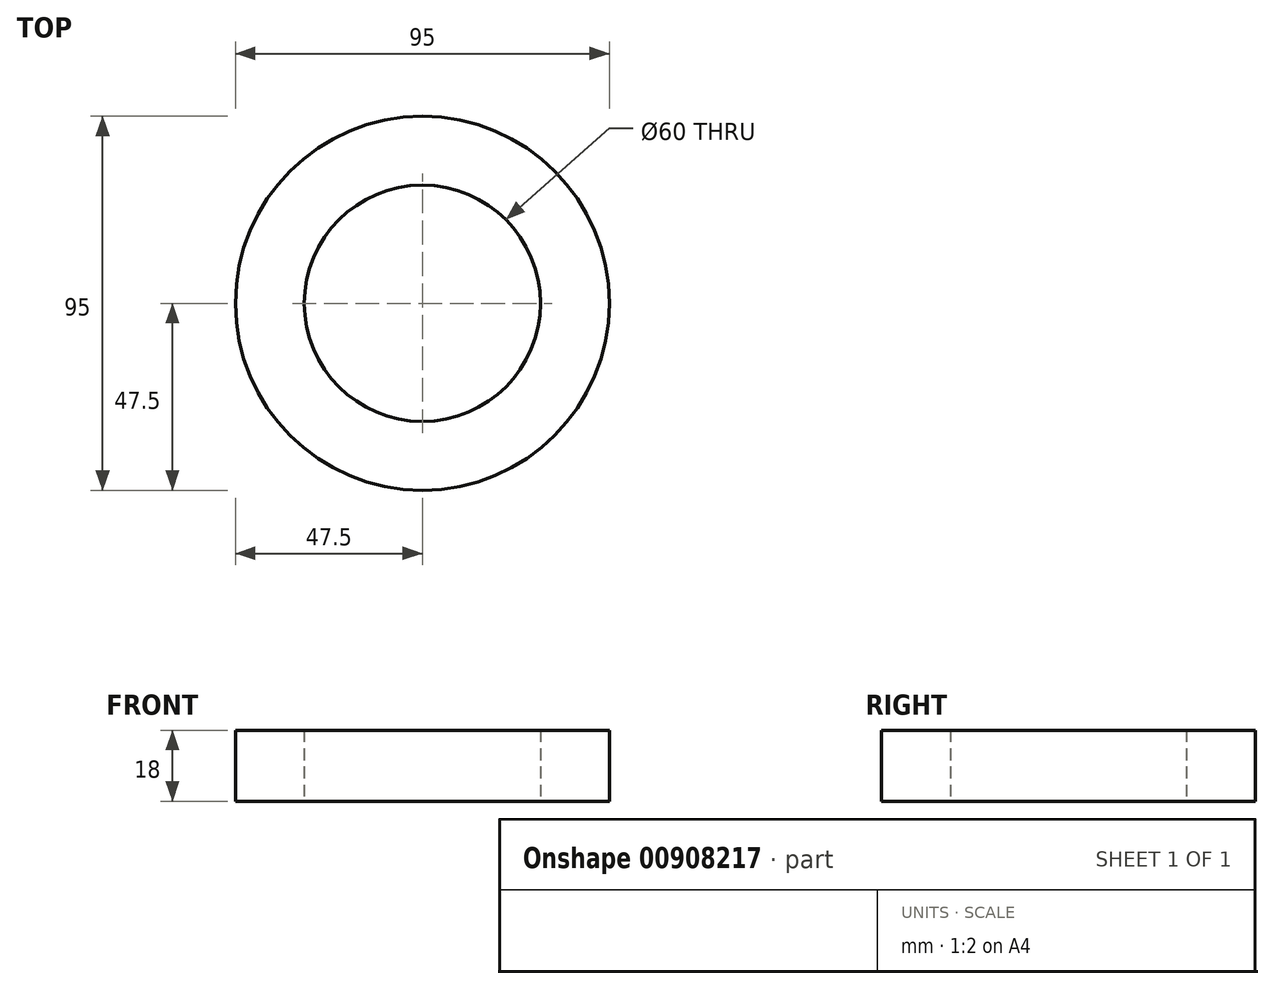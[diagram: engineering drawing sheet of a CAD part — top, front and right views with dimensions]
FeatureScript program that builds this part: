
annotation { "Feature Type Name" : "Feature", "Feature Type Description" : "" }
export const myFeature = defineFeature(function(context is Context, id is Id, definition is map)
    precondition{}
    {
        {
            var Q0;
            Q0=qCreatedBy(makeId("Top.planeOp"),FACE);
            var sketch = newSketch(context, id + "F0", { "sketchPlane" : qUnion([Q0])});
            skCircle(sketch, "E0", {"center": v(0, 0) * mm, "radius": 30 * mm});
            skCircle(sketch, "E1", {"center": v(0, 0) * mm, "radius": 47.5 * mm});
            skSolve(sketch);
        }
        {
            var Q0;
            Q0 = qSketchRegion(id + "F0", true);
            extrude(context, id + "F1", {"entities" : qUnion([Q0]), "depth" : 18 * mm, "offsetDistance" : 25 * mm});
        }
    });
